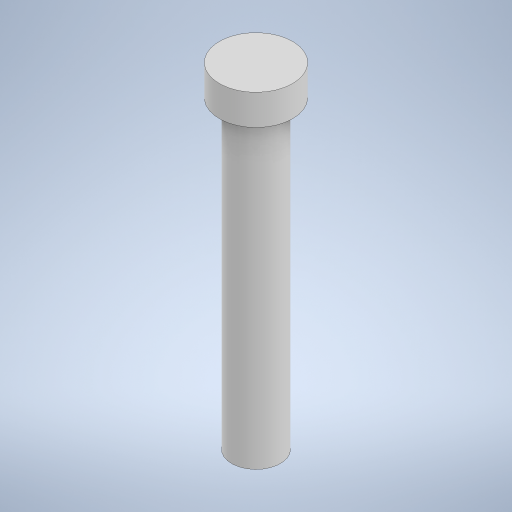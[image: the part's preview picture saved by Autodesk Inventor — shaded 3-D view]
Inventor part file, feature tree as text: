
AUTODESK INVENTOR PART (.ipt)
format: ipt  version: 2024 (Build 280153000, 153)  size: 235,520 bytes
history: native  units: mm
features: extrude x2, sketch x2
ambient origin geometry x8: Origin, YZ Plane, XZ Plane, XY Plane, X Axis, Y Axis, Z Axis, Center Point
bodies: Solid1 (feature_tree)
feature tree (4):
  extrude  "Extrusion1"  Depth=50.0mm TaperAngle=0.0deg
  extrude  "Extrusion2"  Depth=5.0mm TaperAngle=0.0deg
  sketch  "Sketch1"  dims[d0=8.0mm d1=50.0mm d2=0.0mm]
  sketch  "Sketch2"  dims[d3=12.0mm d4=5.0mm d5=0.0mm]
